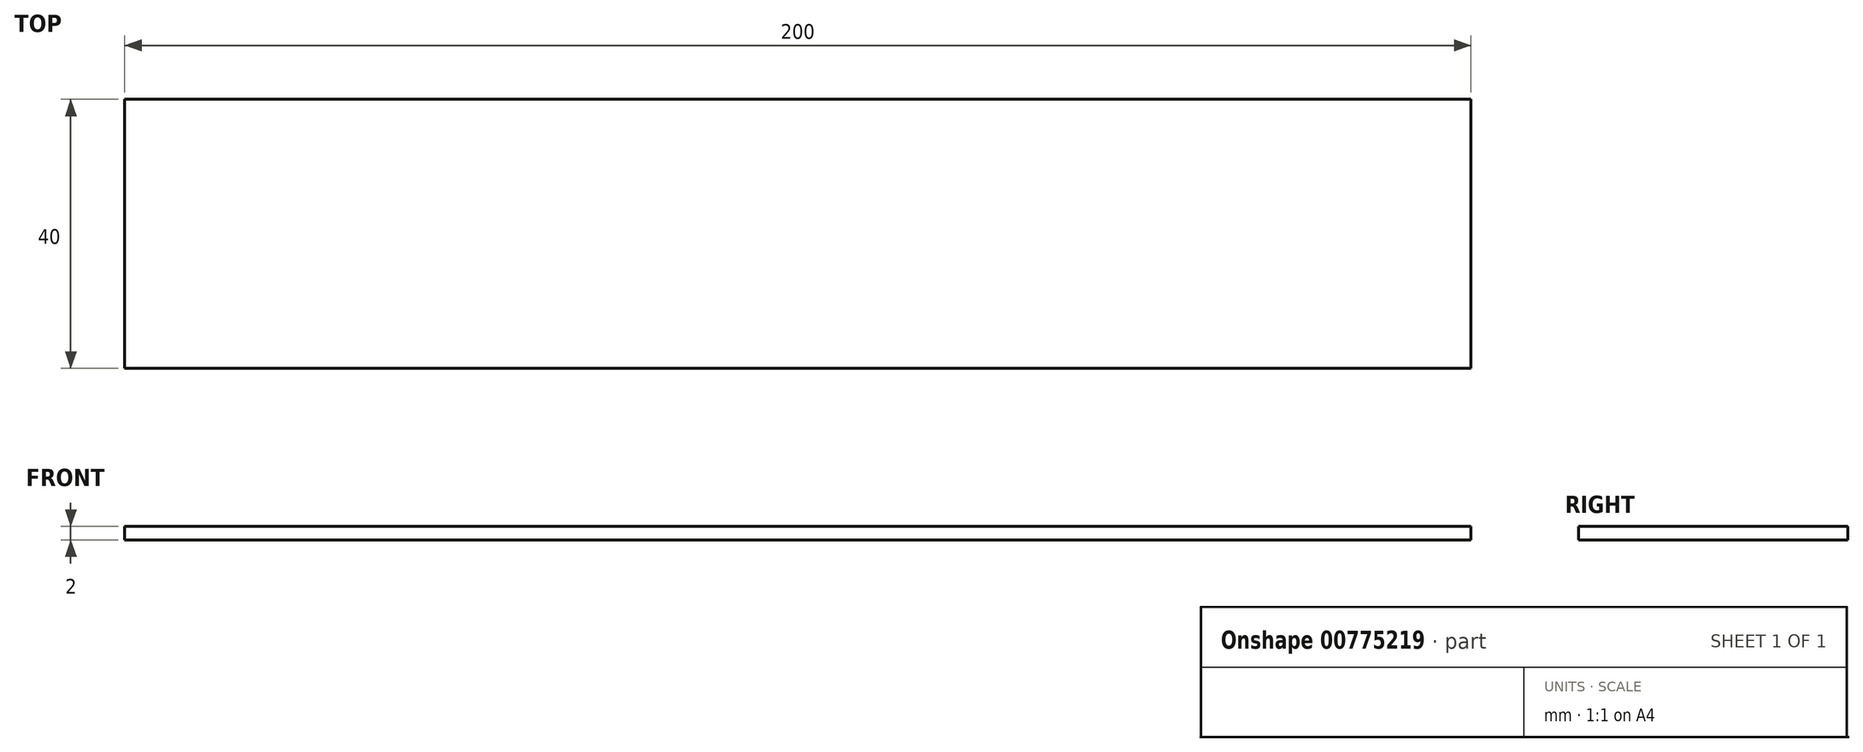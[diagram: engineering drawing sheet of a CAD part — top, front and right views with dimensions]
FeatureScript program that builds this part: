
annotation { "Feature Type Name" : "Feature", "Feature Type Description" : "" }
export const myFeature = defineFeature(function(context is Context, id is Id, definition is map)
    precondition{}
    {
        {
            var Q0;
            Q0=qCreatedBy(makeId("Top.planeOp"),FACE);
            var sketch = newSketch(context, id + "F0", { "sketchPlane" : qUnion([Q0])});
            skLineSegment(sketch, "E0.bottom", {"start": v(-100, -20) * mm, "end": v(100, -20) * mm});
            skLineSegment(sketch, "E0.top", {"start": v(-100, 20) * mm, "end": v(100, 20) * mm});
            skLineSegment(sketch, "E0.left", {"start": v(-100, -20) * mm, "end": v(-100, 20) * mm});
            skLineSegment(sketch, "E0.right", {"start": v(100, -20) * mm, "end": v(100, 20) * mm});
            skPoint(sketch, "E0.middle", {"position": v(0, 0) * mm});
            skSolve(sketch);
        }
        {
            var Q0;
            Q0 = qSketchRegion(id + "F0", true);
            extrude(context, id + "F1", {"entities" : qUnion([Q0]), "depth" : 2 * mm, "offsetDistance" : 25 * mm});
        }
    });
